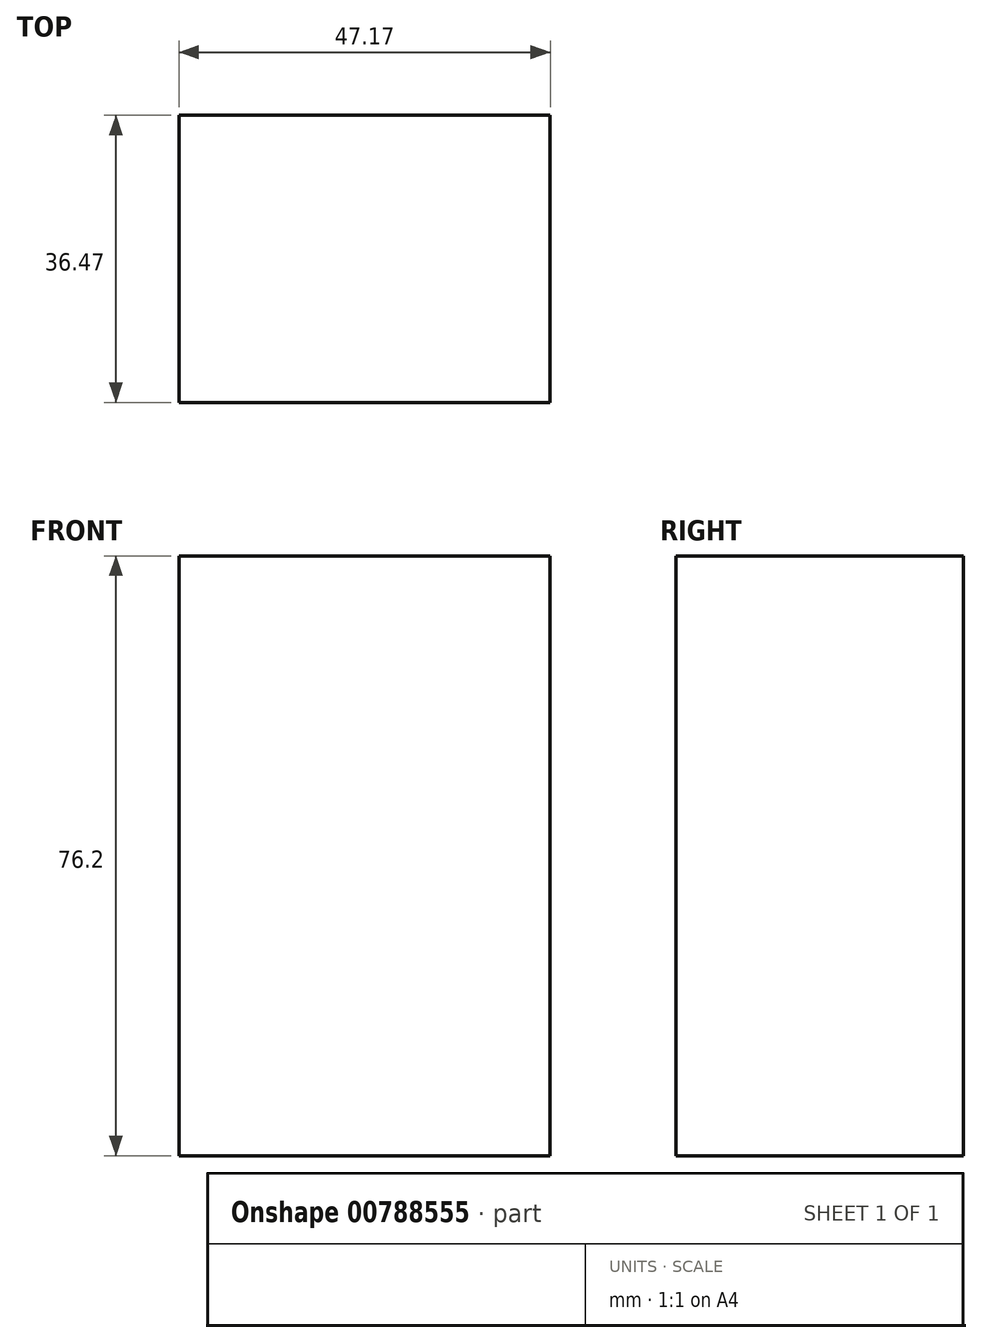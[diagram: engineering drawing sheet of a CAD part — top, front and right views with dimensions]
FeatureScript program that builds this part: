
annotation { "Feature Type Name" : "Feature", "Feature Type Description" : "" }
export const myFeature = defineFeature(function(context is Context, id is Id, definition is map)
    precondition{}
    {
        {
            var Q0;
            Q0=qCreatedBy(makeId("Top.planeOp"),FACE);
            var sketch = newSketch(context, id + "F0", { "sketchPlane" : qUnion([Q0])});
            skLineSegment(sketch, "E0.bottom", {"start": v(-58.9, 46.5) * mm, "end": v(-11.74, 46.5) * mm});
            skLineSegment(sketch, "E0.top", {"start": v(-58.9, 10.03) * mm, "end": v(-11.74, 10.03) * mm});
            skLineSegment(sketch, "E0.left", {"start": v(-58.9, 46.5) * mm, "end": v(-58.9, 10.03) * mm});
            skLineSegment(sketch, "E0.right", {"start": v(-11.74, 46.5) * mm, "end": v(-11.74, 10.03) * mm});
            skSolve(sketch);
        }
        {
            var Q0;
            Q0 = qSketchRegion(id + "F0", true);
            extrude(context, id + "F1", {"entities" : qUnion([Q0]), "depth" : 76.2 * mm, "offsetDistance" : 25.4 * mm});
        }
    });
